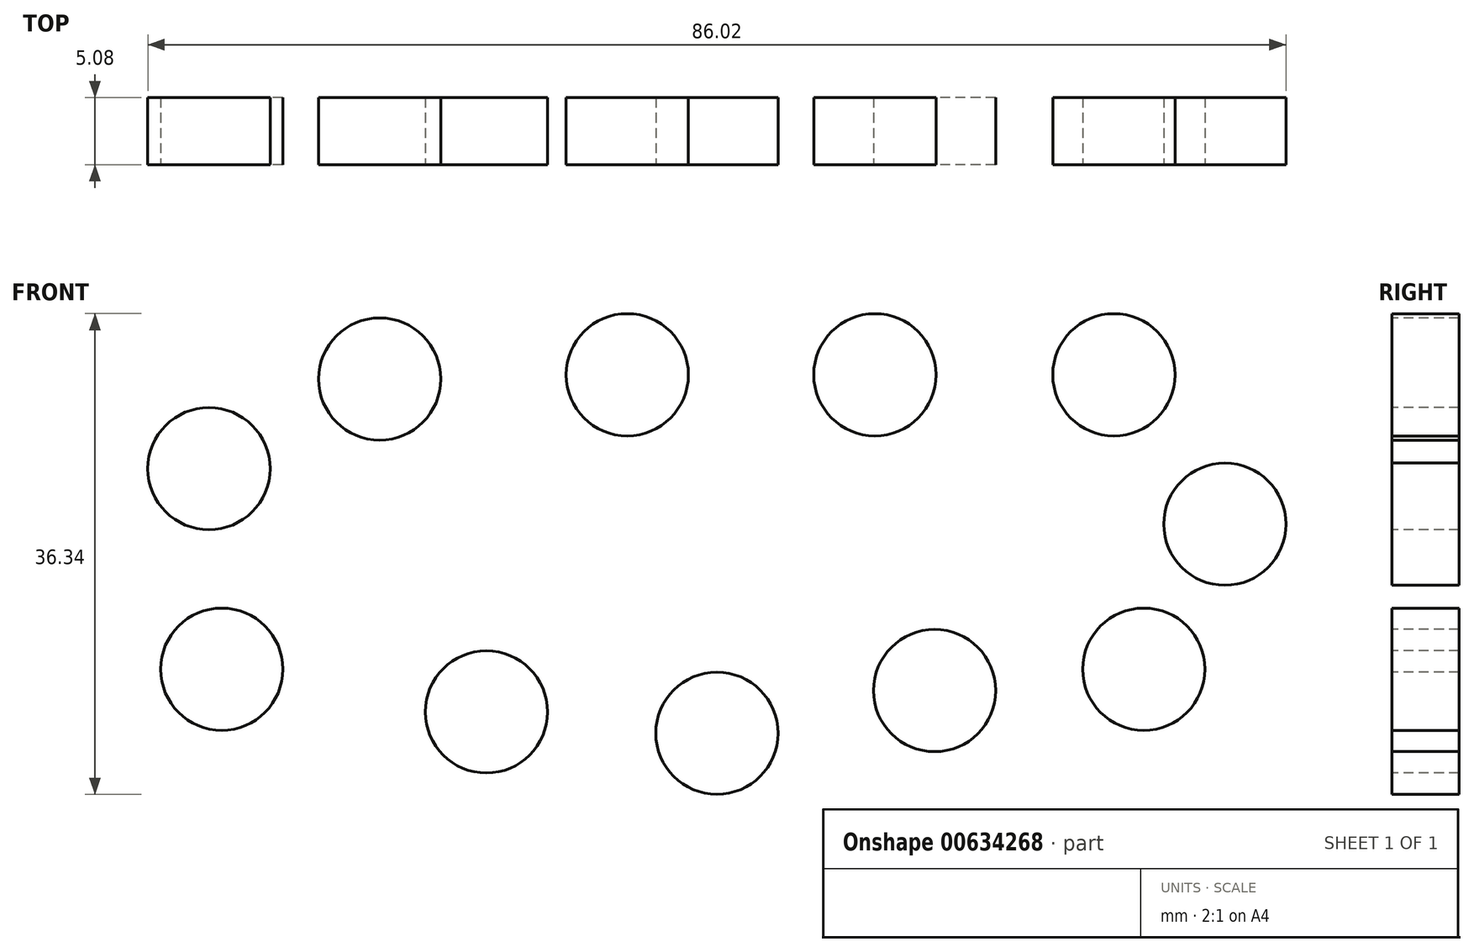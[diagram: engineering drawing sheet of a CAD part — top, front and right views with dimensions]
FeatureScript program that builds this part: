
annotation { "Feature Type Name" : "Feature", "Feature Type Description" : "" }
export const myFeature = defineFeature(function(context is Context, id is Id, definition is map)
    precondition{}
    {
        {
            var Q0;
            Q0=qCreatedBy(makeId("Front.planeOp"),FACE);
            var sketch = newSketch(context, id + "F0", { "sketchPlane" : qUnion([Q0])});
            skCircle(sketch, "E0", {"center": v(-22.72, 20.48) * mm, "radius": 4.62 * mm});
            skCircle(sketch, "E1", {"center": v(-4, 20.8) * mm, "radius": 4.62 * mm});
            skCircle(sketch, "E2", {"center": v(14.7, 20.8) * mm, "radius": 4.62 * mm});
            skCircle(sketch, "E3", {"center": v(32.77, 20.8) * mm, "radius": 4.62 * mm});
            skCircle(sketch, "E4", {"center": v(41.16, 9.52) * mm, "radius": 4.62 * mm});
            skCircle(sketch, "E5", {"center": v(35.03, -1.45) * mm, "radius": 4.62 * mm});
            skCircle(sketch, "E6", {"center": v(19.22, -3.07) * mm, "radius": 4.62 * mm});
            skCircle(sketch, "E7", {"center": v(2.77, -6.3) * mm, "radius": 4.62 * mm});
            skCircle(sketch, "E8", {"center": v(-14.65, -4.68) * mm, "radius": 4.62 * mm});
            skCircle(sketch, "E9", {"center": v(-34.66, -1.45) * mm, "radius": 4.62 * mm});
            skCircle(sketch, "E10", {"center": v(-35.62, 13.7) * mm, "radius": 4.62 * mm});
            skSolve(sketch);
        }
        {
            var Q0;
            Q0=sQuery(id+"F0.wireOp",EDGE,"E2");
            var Q1;
            Q1=sQuery(id+"F0.wireOp",EDGE,"E9");
            var Q2;
            Q2=sQuery(id+"F0.wireOp",EDGE,"E10");
            var Q3;
            Q3=sQuery(id+"F0.wireOp",EDGE,"E3");
            var Q4;
            Q4=sQuery(id+"F0.wireOp",EDGE,"E4");
            var Q5;
            Q5=sQuery(id+"F0.wireOp",EDGE,"E5");
            var Q6;
            Q6=sQuery(id+"F0.wireOp",EDGE,"E1");
            var Q7;
            Q7=sQuery(id+"F0.wireOp",EDGE,"E0");
            var Q8;
            Q8=sQuery(id+"F0.wireOp",EDGE,"E7");
            var Q9;
            Q9=sQuery(id+"F0.wireOp",EDGE,"E6");
            var Q10;
            Q10=sQuery(id+"F0.wireOp",EDGE,"E8");
            extrude(context, id + "F1", {"bodyType" : ToolBodyType.SURFACE, "surfaceEntities" : qUnion([Q0, Q1, Q2, Q3, Q4, Q5, Q6, Q7, Q8, Q9, Q10]), "depth" : 5.08 * mm, "offsetDistance" : 25.4 * mm});
        }
    });
